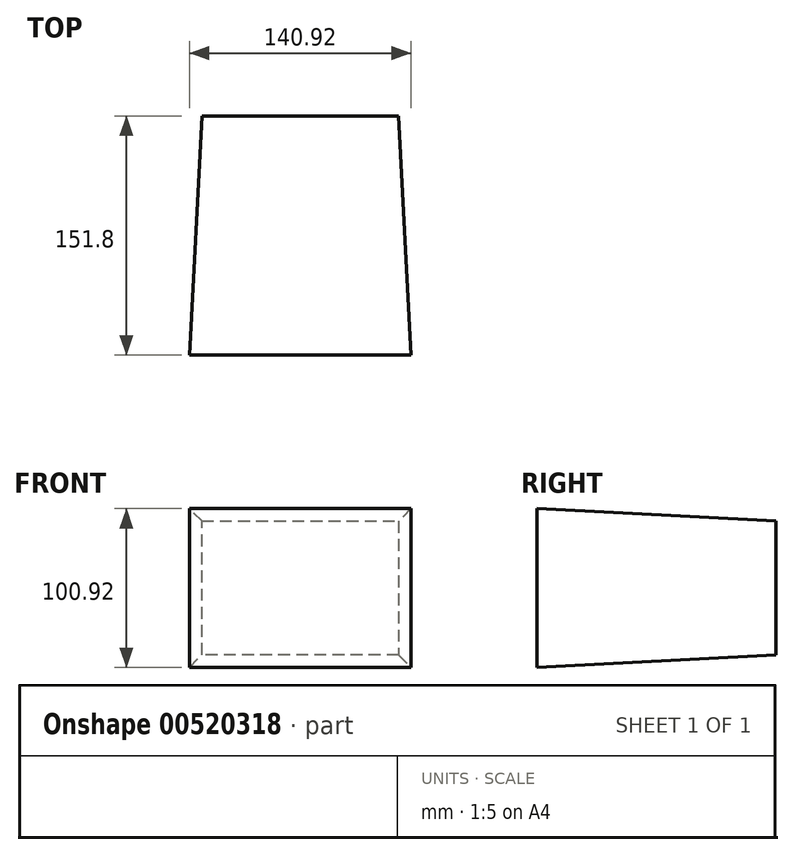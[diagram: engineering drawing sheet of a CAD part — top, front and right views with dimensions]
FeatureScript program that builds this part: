
annotation { "Feature Type Name" : "Feature", "Feature Type Description" : "" }
export const myFeature = defineFeature(function(context is Context, id is Id, definition is map)
    precondition{}
    {
        {
            var Q0;
            Q0=qCreatedBy(makeId("Front.planeOp"),FACE);
            var sketch = newSketch(context, id + "F0", { "sketchPlane" : qUnion([Q0])});
            skLineSegment(sketch, "E0.bottom", {"start": v(-62.5, 42.5) * mm, "end": v(62.5, 42.5) * mm});
            skLineSegment(sketch, "E0.top", {"start": v(-62.5, -42.5) * mm, "end": v(62.5, -42.5) * mm});
            skLineSegment(sketch, "E0.left", {"start": v(-62.5, 42.5) * mm, "end": v(-62.5, -42.5) * mm});
            skLineSegment(sketch, "E0.right", {"start": v(62.5, 42.5) * mm, "end": v(62.5, -42.5) * mm});
            skPoint(sketch, "E0.middle", {"position": v(0, 0) * mm});
            skSolve(sketch);
        }
        {
            var Q0;
            Q0=makeQuery(id+"F0.imprint","IMPRINT",FACE,{"disambiguationData":[TD([[makeQuery(id+"F0.imprint","IMPRINT",EDGE,{"derivedFrom":sQuery(id+"F0.wireOp",EDGE,"E0.bottom")}),-1.0]])]});
            extrude(context, id + "F1", {"entities" : qUnion([Q0]), "depth" : 151.8 * mm, "offsetDistance" : 25 * mm, "hasDraft" : true, "draftAngle" : 3 * degree});
        }
    });
